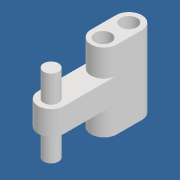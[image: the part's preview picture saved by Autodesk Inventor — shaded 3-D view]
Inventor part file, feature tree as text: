
AUTODESK INVENTOR PART (.ipt)
format: ipt  version: 2020 (Build 240168000, 168)  size: 148,480 bytes
history: native  units: mm
features: extrude x4, sketch x4, fillet x3
ambient origin geometry x8: Origin, YZ Plane, XZ Plane, XY Plane, X Axis, Y Axis, Z Axis, Center Point
bodies: Solid1 (feature_tree)
feature tree (11):
  extrude  "Extrusion1"  Depth=15.7mm
  fillet  "Fillet1"  Radius=5.0mm
  fillet  "Fillet2"  Radius=5.0mm
  extrude  "Extrusion2"  Depth=24.0mm TaperAngle=0.0deg
  extrude  "Extrusion4"  Depth=4.0mm
  fillet  "Fillet3"  Radius=4.0mm
  extrude  "Extrusion5"  Depth=7.4mm
  sketch  "Sketch1"  dims[d0=8.0mm d1=15.7mm d4=5.0mm d5=5.0mm]
  sketch  "Sketch2"  dims[d8=8.0mm d11=24.0mm d12=0.0mm]
  sketch  "Sketch4"  dims[d13=4.0mm d14=4.0mm d15=4.0mm]
  sketch  "Sketch5"  dims[d17=20.3mm d18=7.4mm d19=8.3mm d20=8.0mm d21=0.0mm d24=4.6mm d25=4.0mm d26=4.0mm d27=8.3mm d28=15.7mm d29=0.0mm d30=0.0mm d31=4.0mm d32=8.3mm d33=0.0mm]
